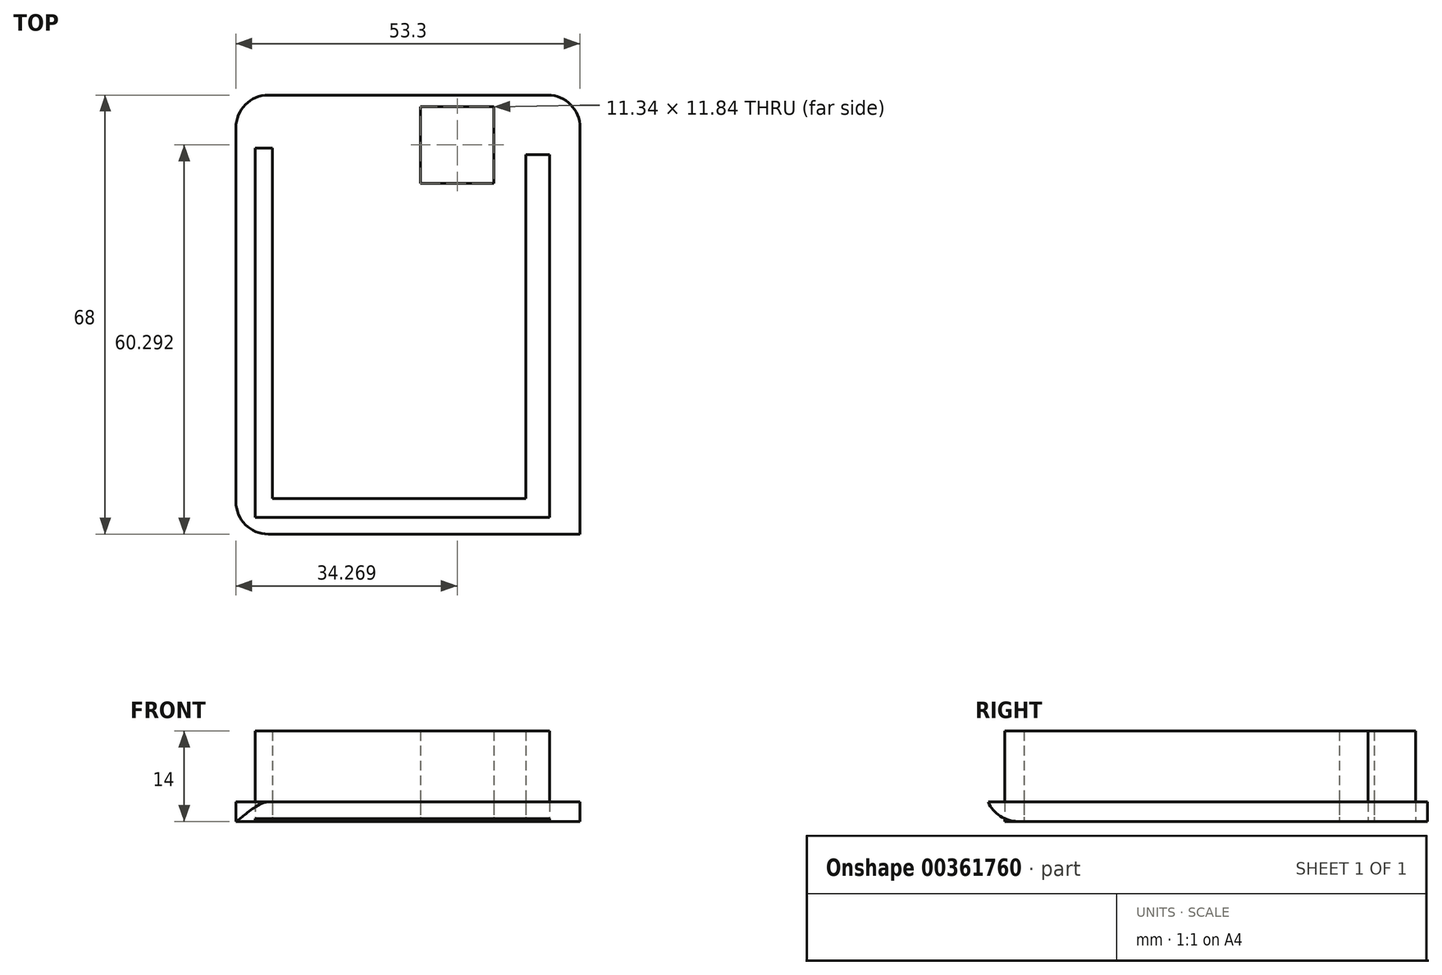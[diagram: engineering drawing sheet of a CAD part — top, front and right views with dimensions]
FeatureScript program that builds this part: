
annotation { "Feature Type Name" : "Feature", "Feature Type Description" : "" }
export const myFeature = defineFeature(function(context is Context, id is Id, definition is map)
    precondition{}
    {
        {
            var Q0;
            Q0=qCreatedBy(makeId("Top.planeOp"),FACE);
            var sketch = newSketch(context, id + "F0", { "sketchPlane" : qUnion([Q0])});
            skLineSegment(sketch, "E0.bottom", {"start": v(-25.93, -23.59) * mm, "end": v(27.37, -23.59) * mm});
            skLineSegment(sketch, "E0.top", {"start": v(-25.93, 44.41) * mm, "end": v(27.37, 44.41) * mm});
            skLineSegment(sketch, "E0.left", {"start": v(-25.93, -23.59) * mm, "end": v(-25.93, 44.41) * mm});
            skLineSegment(sketch, "E0.right", {"start": v(27.37, -23.59) * mm, "end": v(27.37, 44.41) * mm});
            skLineSegment(sketch, "E1.bottom", {"start": v(-22.98, 36.2) * mm, "end": v(-20.27, 36.2) * mm});
            skLineSegment(sketch, "E1.top", {"start": v(-22.98, -21) * mm, "end": v(-20.27, -21) * mm});
            skLineSegment(sketch, "E1.left", {"start": v(-22.98, 36.2) * mm, "end": v(-22.98, -21) * mm});
            skLineSegment(sketch, "E1.right", {"start": v(-20.27, 36.2) * mm, "end": v(-20.27, -18.05) * mm});
            skLineSegment(sketch, "E2.bottom", {"start": v(-20.27, -18.05) * mm, "end": v(18.94, -18.05) * mm});
            skLineSegment(sketch, "E2.top", {"start": v(-22.98, -21) * mm, "end": v(22.64, -21) * mm});
            skLineSegment(sketch, "E2.left", {"start": v(-22.98, -18.05) * mm, "end": v(-22.98, -21) * mm});
            skLineSegment(sketch, "E2.right", {"start": v(22.64, -18.05) * mm, "end": v(22.64, -21) * mm});
            skLineSegment(sketch, "E3.bottom", {"start": v(22.64, -21) * mm, "end": v(18.94, -21) * mm});
            skLineSegment(sketch, "E3.top", {"start": v(22.64, 35.22) * mm, "end": v(18.94, 35.22) * mm});
            skLineSegment(sketch, "E3.left", {"start": v(22.64, -21) * mm, "end": v(22.64, 35.22) * mm});
            skLineSegment(sketch, "E3.right", {"start": v(18.94, -18.05) * mm, "end": v(18.94, 35.22) * mm});
            skLineSegment(sketch, "E4.bottom", {"start": v(14.01, 42.62) * mm, "end": v(2.67, 42.62) * mm});
            skLineSegment(sketch, "E4.top", {"start": v(14.01, 30.78) * mm, "end": v(2.67, 30.78) * mm});
            skLineSegment(sketch, "E4.left", {"start": v(14.01, 42.62) * mm, "end": v(14.01, 30.78) * mm});
            skLineSegment(sketch, "E4.right", {"start": v(2.67, 42.62) * mm, "end": v(2.67, 30.78) * mm});
            skSolve(sketch);
        }
        {
            var Q0;
            Q0=makeQuery(id+"F0.imprint","IMPRINT",FACE,{"disambiguationData":[TD([[makeQuery(id+"F0.imprint","IMPRINT",EDGE,{"derivedFrom":sQuery(id+"F0.wireOp",EDGE,"E1.bottom")}),-1.0]])]});
            var Q1;
            Q1=makeQuery(id+"F0.imprint","IMPRINT",FACE,{"disambiguationData":[TD([[makeQuery(id+"F0.imprint","IMPRINT",EDGE,{"derivedFrom":sQuery(id+"F0.wireOp",EDGE,"E4.bottom")}),1.0]])]});
            extrude(context, id + "F1", {"entities" : qUnion([Q0, Q1]), "depth" : 14 * mm});
        }
        {
            var Q0;
            Q0=makeQuery(id+"F0.imprint","IMPRINT",FACE,{"disambiguationData":[TD([[makeQuery(id+"F0.imprint","IMPRINT",EDGE,{"derivedFrom":sQuery(id+"F0.wireOp",EDGE,"E0.bottom")}),1.0]])]});
            extrude(context, id + "F2", {"entities" : qUnion([Q0]), "depth" : 3 * mm});
        }
        {
            var Q0;
            Q0=makeQuery(id+"F2.opExtrude","SWEPT_EDGE",EDGE,{"disambiguationData":[OSD([sQuery(id+"F0.wireOp",EDGE,"E0.top"),sQuery(id+"F0.wireOp",EDGE,"E0.left")])]});
            var Q1;
            Q1=makeQuery(id+"F2.opExtrude","SWEPT_EDGE",EDGE,{"disambiguationData":[OSD([sQuery(id+"F0.wireOp",EDGE,"E0.bottom"),sQuery(id+"F0.wireOp",EDGE,"E0.left")])]});
            var Q2;
            Q2=makeQuery(id+"F2.opExtrude","CAP_EDGE",EDGE,{"disambiguationData":[OSD([sQuery(id+"F0.wireOp",EDGE,"E0.bottom")])],"isStart":true});
            var Q3;
            Q3=makeQuery(id+"F2.opExtrude","SWEPT_EDGE",EDGE,{"disambiguationData":[OSD([sQuery(id+"F0.wireOp",EDGE,"E0.top"),sQuery(id+"F0.wireOp",EDGE,"E0.right")])]});
            fillet(context, id + "F3", {"entities" : qUnion([Q0, Q1, Q2, Q3]), "radius" : 5 * mm, "tangentPropagation" : true, "allowEdgeOverflow" : false});
        }
    });
